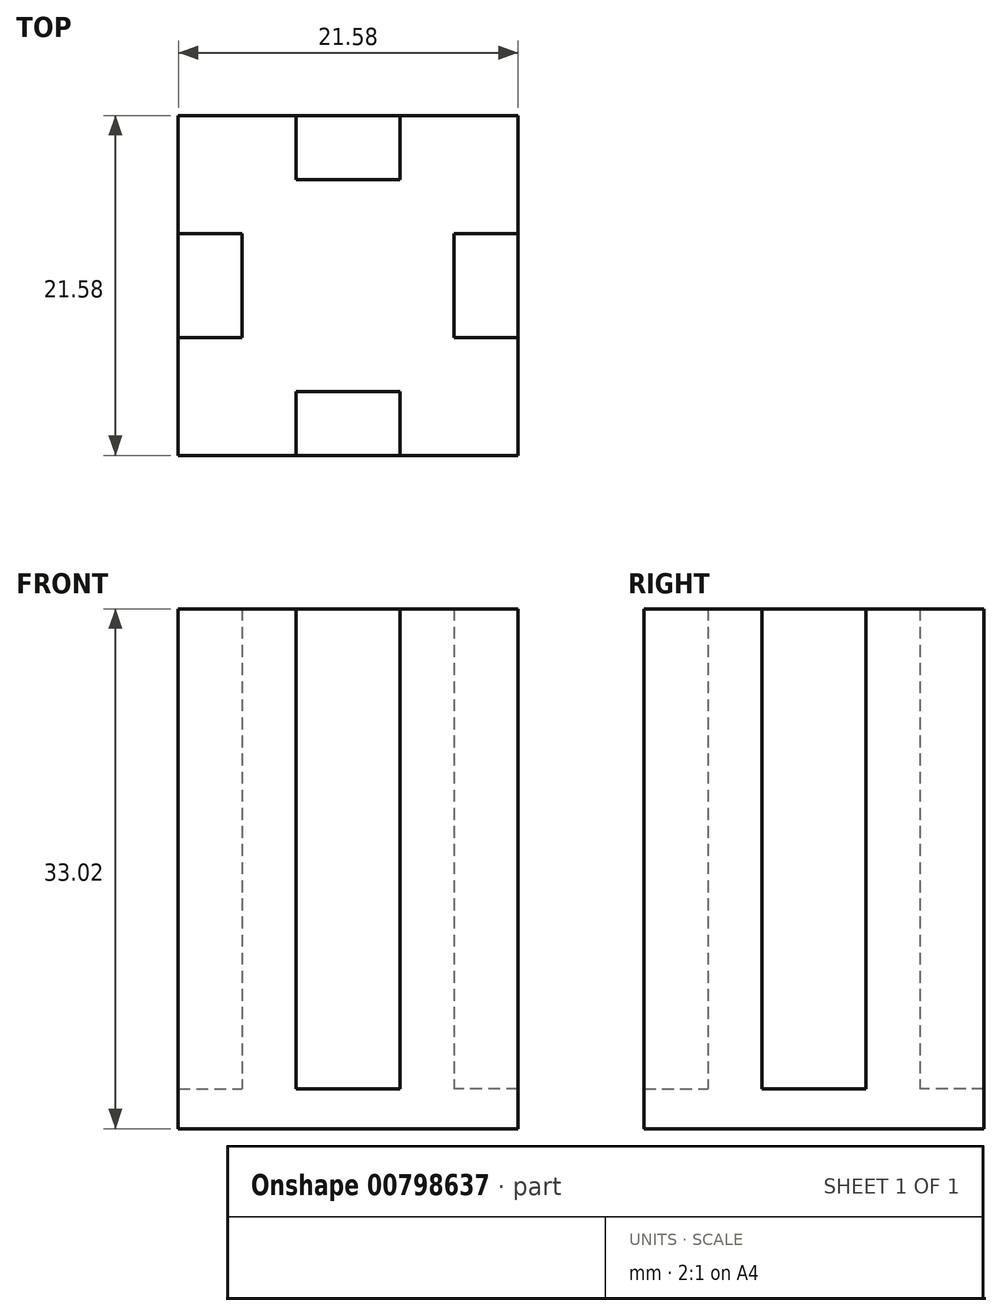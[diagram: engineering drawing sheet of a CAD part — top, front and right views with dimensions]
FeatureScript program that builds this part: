
annotation { "Feature Type Name" : "Feature", "Feature Type Description" : "" }
export const myFeature = defineFeature(function(context is Context, id is Id, definition is map)
    precondition{}
    {
        {
            var Q0;
            Q0=qCreatedBy(makeId("Top.planeOp"),FACE);
            var sketch = newSketch(context, id + "F0", { "sketchPlane" : qUnion([Q0])});
            skLineSegment(sketch, "E0.bottom", {"start": v(-10.8, 10.8) * mm, "end": v(10.8, 10.8) * mm});
            skLineSegment(sketch, "E0.top", {"start": v(-10.8, -10.8) * mm, "end": v(10.8, -10.8) * mm});
            skLineSegment(sketch, "E0.left", {"start": v(-10.8, 10.8) * mm, "end": v(-10.8, -10.8) * mm});
            skLineSegment(sketch, "E0.right", {"start": v(10.8, 10.8) * mm, "end": v(10.8, -10.8) * mm});
            skPoint(sketch, "E0.middle", {"position": v(0, 0) * mm});
            skLineSegment(sketch, "E1.bottom", {"start": v(-10.8, 3.3) * mm, "end": v(-6.73, 3.3) * mm});
            skLineSegment(sketch, "E1.top", {"start": v(-10.8, -3.3) * mm, "end": v(-6.73, -3.3) * mm});
            skLineSegment(sketch, "E1.left", {"start": v(-10.8, 3.3) * mm, "end": v(-10.8, -3.3) * mm});
            skLineSegment(sketch, "E1.right", {"start": v(-6.73, 3.3) * mm, "end": v(-6.73, -3.3) * mm});
            skPoint(sketch, "E1.middle", {"position": v(-8.76, 0) * mm});
            skLineSegment(sketch, "E2.bottom", {"start": v(10.8, 3.3) * mm, "end": v(6.73, 3.3) * mm});
            skLineSegment(sketch, "E2.top", {"start": v(10.8, -3.3) * mm, "end": v(6.73, -3.3) * mm});
            skLineSegment(sketch, "E2.left", {"start": v(10.8, 3.3) * mm, "end": v(10.8, -3.3) * mm});
            skLineSegment(sketch, "E2.right", {"start": v(6.73, 3.3) * mm, "end": v(6.73, -3.3) * mm});
            skPoint(sketch, "E2.middle", {"position": v(8.76, 0) * mm});
            skLineSegment(sketch, "E3.bottom", {"start": v(3.3, 10.8) * mm, "end": v(-3.3, 10.8) * mm});
            skLineSegment(sketch, "E3.top", {"start": v(3.3, 6.73) * mm, "end": v(-3.3, 6.73) * mm});
            skLineSegment(sketch, "E3.left", {"start": v(3.3, 10.8) * mm, "end": v(3.3, 6.73) * mm});
            skLineSegment(sketch, "E3.right", {"start": v(-3.3, 10.8) * mm, "end": v(-3.3, 6.73) * mm});
            skPoint(sketch, "E3.middle", {"position": v(0, 8.76) * mm});
            skPoint(sketch, "E3.middle.positionSnap0", {"position": v(0, 10.8) * mm});
            skPoint(sketch, "E3.centerSnap0", {"position": v(0, 10.8) * mm});
            skLineSegment(sketch, "E4.bottom", {"start": v(3.3, -10.8) * mm, "end": v(-3.3, -10.8) * mm});
            skLineSegment(sketch, "E4.top", {"start": v(3.3, -6.73) * mm, "end": v(-3.3, -6.73) * mm});
            skLineSegment(sketch, "E4.left", {"start": v(3.3, -10.8) * mm, "end": v(3.3, -6.73) * mm});
            skLineSegment(sketch, "E4.right", {"start": v(-3.3, -10.8) * mm, "end": v(-3.3, -6.73) * mm});
            skPoint(sketch, "E4.middle", {"position": v(0, -8.76) * mm});
            skSolve(sketch);
        }
        {
            var Q0;
            {var subQ8=sQuery(id+"F0.wireOp",EDGE,"E1.bottom");Q0=makeQuery(id+"F0.imprint","IMPRINT",FACE,{"disambiguationData":[TD([[makeQuery(id+"F0.imprint","IMPRINT",EDGE,{"derivedFrom":subQ8}),1.0]])]});}
            extrude(context, id + "F1", {"entities" : qUnion([Q0]), "depth" : 33.02 * mm, "offsetDistance" : 25.4 * mm});
        }
        {
            var Q0;
            {var subQ2=sQuery(id+"F0.wireOp",EDGE,"E1.bottom");Q0=makeQuery(id+"F0.imprint","IMPRINT",FACE,{"disambiguationData":[TD([[makeQuery(id+"F0.imprint","IMPRINT",EDGE,{"derivedFrom":subQ2}),-1.0]])]});}
            var Q1;
            Q1=makeQuery(id+"F0.imprint","IMPRINT",FACE,{"disambiguationData":[TD([[makeQuery(id+"F0.imprint","IMPRINT",EDGE,{"derivedFrom":sQuery(id+"F0.wireOp",EDGE,"E3.top")}),-1.0]])]});
            var Q2;
            {var subQ2=sQuery(id+"F0.wireOp",EDGE,"E2.bottom");Q2=makeQuery(id+"F0.imprint","IMPRINT",FACE,{"disambiguationData":[TD([[makeQuery(id+"F0.imprint","IMPRINT",EDGE,{"derivedFrom":subQ2}),1.0]])]});}
            var Q3;
            Q3=makeQuery(id+"F0.imprint","IMPRINT",FACE,{"disambiguationData":[TD([[makeQuery(id+"F0.imprint","IMPRINT",EDGE,{"derivedFrom":sQuery(id+"F0.wireOp",EDGE,"E4.top")}),1.0]])]});
            extrude(context, id + "F2", {"entities" : qUnion([Q0, Q1, Q2, Q3]), "operationType" : NewBodyOperationType.ADD, "depth" : 2.54 * mm, "offsetDistance" : 25.4 * mm});
        }
    });
